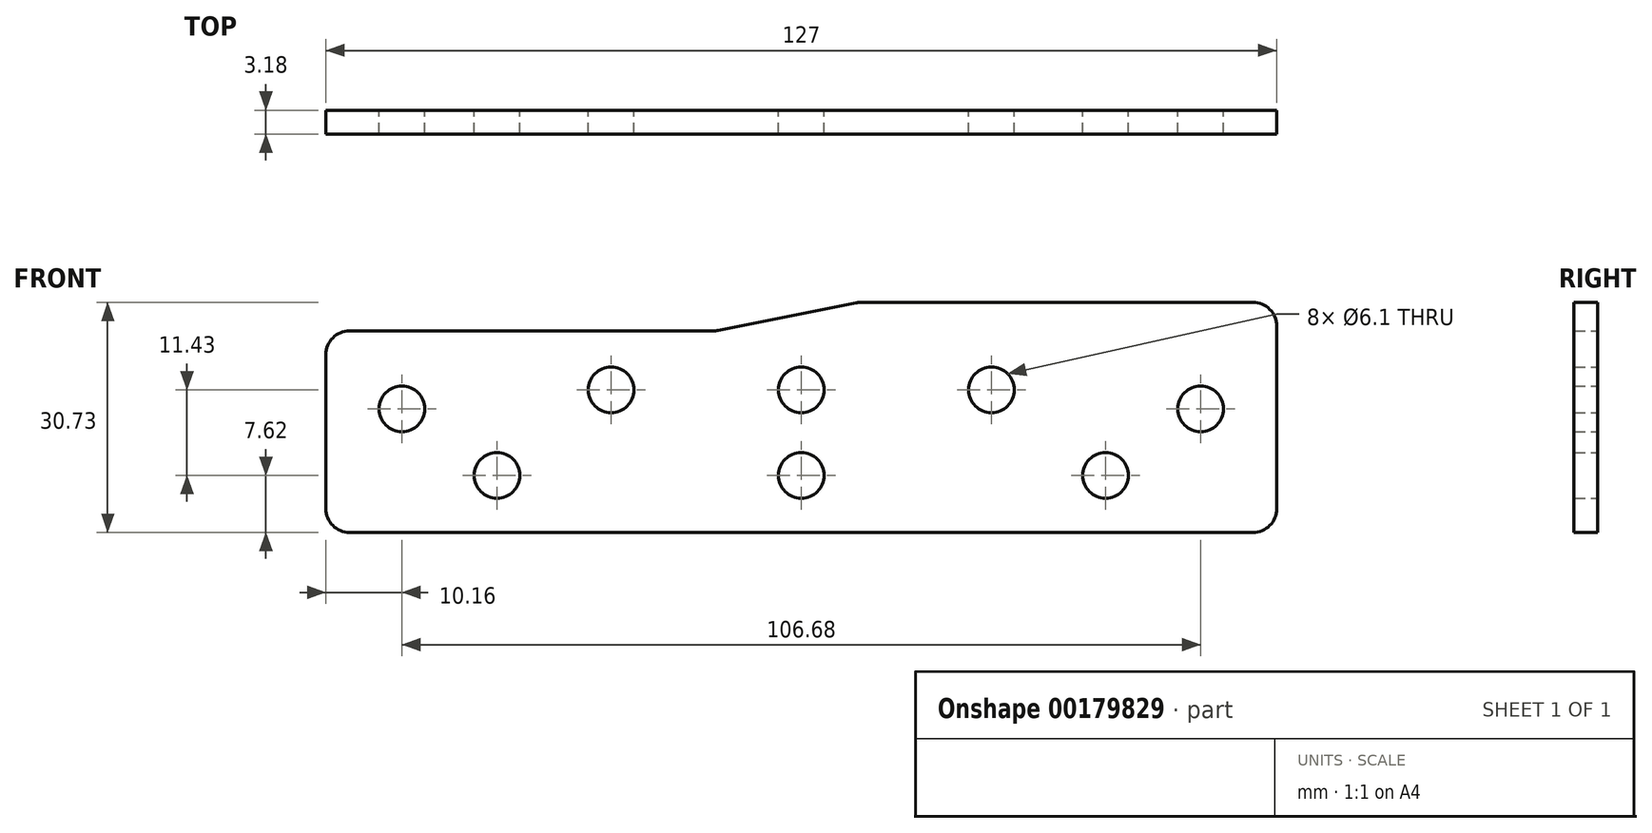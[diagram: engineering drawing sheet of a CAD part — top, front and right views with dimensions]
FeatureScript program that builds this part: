
annotation { "Feature Type Name" : "Feature", "Feature Type Description" : "" }
export const myFeature = defineFeature(function(context is Context, id is Id, definition is map)
    precondition{}
    {
        {
            var Q0;
            Q0=qCreatedBy(makeId("Front.planeOp"),FACE);
            var sketch = newSketch(context, id + "F0", { "sketchPlane" : qUnion([Q0])});
            skLineSegment(sketch, "E0.top", {"start": v(-60.33, 0) * mm, "end": v(60.33, 0) * mm});
            skLineSegment(sketch, "E0.right", {"start": v(63.5, 27.56) * mm, "end": v(63.5, 3.18) * mm});
            skLineSegment(sketch, "E1", {"start": v(-60.33, 26.92) * mm, "end": v(-11.43, 26.92) * mm});
            skLineSegment(sketch, "E2", {"start": v(-11.43, 26.92) * mm, "end": v(7.62, 30.73) * mm});
            skLineSegment(sketch, "E3", {"start": v(60.33, 30.73) * mm, "end": v(7.62, 30.73) * mm});
            skLineSegment(sketch, "E4", {"start": v(-63.5, 23.75) * mm, "end": v(-63.5, 3.17) * mm});
            skPoint(sketch, "E5.visualSharp", {"position": v(-63.5, 26.92) * mm});
            skPoint(sketch, "E6.visualSharp", {"position": v(63.5, 30.73) * mm});
            skPoint(sketch, "E7.visualSharp", {"position": v(63.5, 0) * mm});
            skPoint(sketch, "E8.visualSharp", {"position": v(-63.5, 0) * mm});
            skCircle(sketch, "E9", {"center": v(-40.64, 7.62) * mm, "radius": 3.05 * mm});
            skCircle(sketch, "E10", {"center": v(0, 7.62) * mm, "radius": 3.05 * mm});
            skCircle(sketch, "E11", {"center": v(53.34, 16.5) * mm, "radius": 3.05 * mm});
            skCircle(sketch, "E12", {"center": v(25.4, 19.05) * mm, "radius": 3.05 * mm});
            skCircle(sketch, "E13", {"center": v(0, 19.05) * mm, "radius": 3.05 * mm});
            skCircle(sketch, "E14", {"center": v(-25.4, 19.05) * mm, "radius": 3.05 * mm});
            skCircle(sketch, "E15", {"center": v(-53.34, 16.5) * mm, "radius": 3.05 * mm});
            skCircle(sketch, "E16", {"center": v(40.64, 7.62) * mm, "radius": 3.05 * mm});
            skArc(sketch, "E17.filletArc", {"start": v(-63.5, 3.17) * mm, "mid": v(-62.57, 0.93) * mm, "end": v(-60.33, 0) * mm});
            skArc(sketch, "E18.filletArc", {"start": v(-60.33, 26.92) * mm, "mid": v(-62.57, 26) * mm, "end": v(-63.5, 23.75) * mm});
            skArc(sketch, "E19.filletArc", {"start": v(60.33, 0) * mm, "mid": v(62.57, 0.93) * mm, "end": v(63.5, 3.18) * mm});
            skArc(sketch, "E20.filletArc", {"start": v(63.5, 27.56) * mm, "mid": v(62.57, 29.8) * mm, "end": v(60.33, 30.73) * mm});
            skSolve(sketch);
        }
        {
            var Q0;
            Q0=makeQuery(id+"F0.imprint","IMPRINT",FACE,{"disambiguationData":[TD([[makeQuery(id+"F0.imprint","IMPRINT",EDGE,{"derivedFrom":sQuery(id+"F0.wireOp",EDGE,"E0.top")}),1.0]])]});
            extrude(context, id + "F1", {"entities" : qUnion([Q0]), "depth" : 3.17 * mm});
        }
        {
            var Q0;
            Q0=makeQuery(id+"F1.opExtrude","SWEPT_EDGE",EDGE,{"disambiguationData":[OSD([sQuery(id+"F0.wireOp",EDGE,"E1"),sQuery(id+"F0.wireOp",EDGE,"E2")])]});
            var Q1;
            Q1=makeQuery(id+"F1.opExtrude","SWEPT_EDGE",EDGE,{"disambiguationData":[OSD([sQuery(id+"F0.wireOp",EDGE,"E2"),sQuery(id+"F0.wireOp",EDGE,"E3")])]});
            fillet(context, id + "F2", {"entities" : qUnion([Q0, Q1]), "radius" : 3.17 * mm, "tangentPropagation" : true, "allowEdgeOverflow" : false});
        }
    });
